# Revit family: Drain_Trench_12_Inch_Wide_Reveal-Zurn-ZF812
name_source: partatom
category: Plumbing Fixtures
units: mm (PartAtom-declared; Revit-internal decimal feet)

## family parameters
Always vertical = Yes
Cut with Voids When Loaded = No
Maintain Annotation Orientation = No
OmniClass Number = 23.70.50.21
OmniClass Title = Liquid Waste Collection and Removal
Part Type = Normal
Room Calculation Point = No
Round Connector Dimension = Use Diameter
Shared = No
Work Plane-Based = No

## types (65) — shared parameters
Approx. Weight (lbs) = 50
Assembly Code = D2040300
Bottom Outlet Connection Extension = 1.063 "
CW Connection = No
Channel Radius Shallow = 3 "
Channel Shallow Radius Exterior = 3.188 "
Connector Thickness 1 = 0.188 "
Description = 12 [305] WIDE REVEAL FIBER REINFORCED POLYMER TRENCH DRAIN SYSTEM WITH STEEL FRAME
Frame Material = Steel - Carbon - Zurn - Painted Black
Grate Material = Iron - Zurn - Cast - Ductile - Painted Black
Grate Thickness = 1.5 "
HW Connection = No
Length = 10 "
Main Material = Polymer - Zurn - Fiber Reinforced - Blue
Manufacturer = Zurn Water, LLC
Manufacurer Brand = Zurn
Model = ZF812
Modified Date = 08/14/2025
Product Documentation Link = https://files.zurn.com
Product Installation Sheet URL = https://files.zurn.com
Product Page URL = https://www.zurn.com
Product data url = https://www.bimobject.com
Trap Primer = No
Type Image = <None>
URL = www.zurn.com
Vent Connection = No
Waste Connection = Yes
angle = 149.00°
zero-valued in all types: CWFU, Default Elevation, HWFU, WFU

## per-type parameters (varying)
| type | Anno-Extension for Endoutlet | Anno-Extension-Deep | Anno-ID | Bottom Connector Length | Bottom Outlet Connection | Deep Invert | End Connector Bottom Length | End Outlet Connection | Flow Rate (GPM) | Outlet Radius | Outlet Radius Exterior | Shallow Invert | Slope Constraints | Trench_Drain-Zurn-ZF812-Bottom_Outlet | Trench_Drain-Zurn-ZF812-End_Outlet | Type Comments |
| ZF812-2002 | 7.992 " | 7.932 " | 2 " | 8.741 " | 2 " | 9.18 " | 9.18 " | 2 " | 937 GPM | 1 " | 1.188 " | 7.93 " | 0.60° | No | No | ZF812-2002 |
| ZF812-2002 W/-E4 | 6.992 " | 7.932 " | 4 " | 8.741 " | 4 " | 9.18 " | 9.18 " | 4 " | 0 GPM | 2 " | 2.188 " | 7.93 " | 0.60° | No | Yes | ZF812-2002 with 4 Inch No-Hub End Outlet |
| ZF812-2002 W/-E6 | 5.992 " | 7.932 " | 6 " | 8.741 " | 6 " | 9.18 " | 9.18 " | 6 " | 0 GPM | 3 " | 3.188 " | 7.93 " | 0.60° | No | Yes | ZF812-2002 with 6 Inch No-Hub End Outlet |
| ZF812-2002 W/-U4 | 6.992 " | 7.932 " | 4 " | 8.741 " | 4 " | 9.18 " | 9.18 " | 4 " | 0 GPM | 2 " | 2.188 " | 7.93 " | 0.60° | Yes | No | ZF812-2002 with 4 Inch No-Hub Bottom Outlet |
| ZF812-2002 W/-U6 | 5.992 " | 7.932 " | 6 " | 8.741 " | 6 " | 9.18 " | 9.18 " | 6 " | 0 GPM | 3 " | 3.188 " | 7.93 " | 0.60° | Yes | No | ZF812-2002 with 6 Inch No-Hub Bottom Outlet |
| ZF812-2002 W/-U8 | 4.992 " | 7.932 " | 8 " | 8.741 " | 8 " | 9.18 " | 9.18 " | 8 " | 0 GPM | 4 " | 4.188 " | 7.93 " | 0.60° | Yes | No | ZF812-2002 with 8 Inch No-Hub Bottom Outlet |
| ZF812-2002N | 7.992 " | 7.932 " | 2 " | 8.741 " | 2 " | 9.18 " | 9.18 " | 2 " | 0 GPM | 1 " | 1.188 " | 9.18 " | 0.00° | No | No | ZF812-2002N |
| ZF812-2003 | 9.242 " | 9.182 " | 2 " | 9.991 " | 2 " | 10.43 " | 10.43 " | 2 " | 1225 GPM | 1 " | 1.188 " | 9.18 " | 0.60° | No | No | ZF812-2003 |
| ZF812-2003 W/-E4 | 8.242 " | 9.182 " | 4 " | 9.991 " | 4 " | 10.43 " | 10.43 " | 4 " | 0 GPM | 2 " | 2.188 " | 9.18 " | 0.60° | No | Yes | ZF812-2003 with 4 Inch No-Hub End Outlet |
| ZF812-2003 W/-E6 | 7.242 " | 9.182 " | 6 " | 9.991 " | 6 " | 10.43 " | 10.43 " | 6 " | 0 GPM | 3 " | 3.188 " | 9.18 " | 0.60° | No | Yes | ZF812-2003 with 6 Inch No-Hub End Outlet |
| ZF812-2003 W/-E8 | 6.242 " | 9.182 " | 8 " | 9.991 " | 8 " | 10.43 " | 10.43 " | 8 " | 0 GPM | 4 " | 4.188 " | 9.18 " | 0.60° | No | Yes | ZF812-2003 with 8 Inch No-Hub End Outlet |
| ZF812-2003 W/-U4 | 8.242 " | 9.182 " | 4 " | 9.991 " | 4 " | 10.43 " | 10.43 " | 4 " | 0 GPM | 2 " | 2.188 " | 9.18 " | 0.60° | Yes | No | ZF812-2003 with 4 Inch No-Hub Bottom Outlet |
| ZF812-2003 W/-U6 | 7.242 " | 9.182 " | 6 " | 9.991 " | 6 " | 10.43 " | 10.43 " | 6 " | 0 GPM | 3 " | 3.188 " | 9.18 " | 0.60° | Yes | No | ZF812-2003 with 6 Inch No-Hub Bottom Outlet |
| ZF812-2003 W/-U8 | 6.242 " | 9.182 " | 8 " | 9.991 " | 8 " | 10.43 " | 10.43 " | 8 " | 0 GPM | 4 " | 4.188 " | 9.18 " | 0.60° | Yes | No | ZF812-2003 with 8 Inch No-Hub Bottom Outlet |
| ZF812-2004 | 10.492 " | 10.432 " | 2 " | 11.241 " | 2 " | 11.68 " | 11.68 " | 2 " | 1521 GPM | 1 " | 1.188 " | 10.43 " | 0.60° | No | No | ZF812-2004 |
| ZF812-2004 W/-E4 | 9.492 " | 10.432 " | 4 " | 11.241 " | 4 " | 11.68 " | 11.68 " | 4 " | 0 GPM | 2 " | 2.188 " | 10.43 " | 0.60° | No | Yes | ZF812-2004 with 4 Inch No-Hub End Outlet |
| ZF812-2004 W/-E6 | 8.492 " | 10.432 " | 6 " | 11.241 " | 6 " | 11.68 " | 11.68 " | 6 " | 0 GPM | 3 " | 3.188 " | 10.43 " | 0.60° | No | Yes | ZF812-2004 with 6 Inch No-Hub End Outlet |
| ZF812-2004 W/-E8 | 7.492 " | 10.432 " | 8 " | 11.241 " | 8 " | 11.68 " | 11.68 " | 8 " | 0 GPM | 4 " | 4.188 " | 10.43 " | 0.60° | No | Yes | ZF812-2004 with 8 Inch No-Hub End Outlet |
| ZF812-2004 W/-U4 | 9.492 " | 10.432 " | 4 " | 11.241 " | 4 " | 11.68 " | 11.68 " | 4 " | 0 GPM | 2 " | 2.188 " | 10.43 " | 0.60° | Yes | No | ZF812-2004 with 4 Inch No-Hub Bottom Outlet |
| ZF812-2004 W/-U6 | 8.492 " | 10.432 " | 6 " | 11.241 " | 6 " | 11.68 " | 11.68 " | 6 " | 0 GPM | 3 " | 3.188 " | 10.43 " | 0.60° | Yes | No | ZF812-2004 with 6 Inch No-Hub Bottom Outlet |
| ZF812-2004 W/-U8 | 7.492 " | 10.432 " | 8 " | 11.241 " | 8 " | 11.68 " | 11.68 " | 8 " | 0 GPM | 4 " | 4.188 " | 10.43 " | 0.60° | Yes | No | ZF812-2004 with 8 Inch No-Hub Bottom Outlet |
| ZF812-2004N | 10.492 " | 10.432 " | 2 " | 11.241 " | 2 " | 11.68 " | 11.68 " | 2 " | 0 GPM | 1 " | 1.188 " | 11.68 " | 0.00° | No | No | ZF812-2004N |
| ZF812-2005 | 11.742 " | 11.682 " | 2 " | 12.491 " | 2 " | 12.93 " | 12.93 " | 2 " | 1821 GPM | 1 " | 1.188 " | 11.68 " | 0.60° | No | No | ZF812-2005 |
| ZF812-2005 W/-E4 | 10.742 " | 11.682 " | 4 " | 12.491 " | 4 " | 12.93 " | 12.93 " | 4 " | 0 GPM | 2 " | 2.188 " | 11.68 " | 0.60° | No | Yes | ZF812-2005 with 4 Inch No-Hub End Outlet |
| ZF812-2005 W/-E6 | 9.742 " | 11.682 " | 6 " | 12.491 " | 6 " | 12.93 " | 12.93 " | 6 " | 0 GPM | 3 " | 3.188 " | 11.68 " | 0.60° | No | Yes | ZF812-2005 with 6 Inch No-Hub End Outlet |
| ZF812-2005 W/-E8 | 8.742 " | 11.682 " | 8 " | 12.491 " | 8 " | 12.93 " | 12.93 " | 8 " | 0 GPM | 4 " | 4.188 " | 11.68 " | 0.60° | No | Yes | ZF812-2005 with 8 Inch No-Hub End Outlet |
| ZF812-2005 W/-U4 | 10.742 " | 11.682 " | 4 " | 12.491 " | 4 " | 12.93 " | 12.93 " | 4 " | 0 GPM | 2 " | 2.188 " | 11.68 " | 0.60° | Yes | No | ZF812-2005 with 4 Inch No-Hub Bottom Outlet |
| ZF812-2005 W/-U6 | 9.742 " | 11.682 " | 6 " | 12.491 " | 6 " | 12.93 " | 12.93 " | 6 " | 0 GPM | 3 " | 3.188 " | 11.68 " | 0.60° | Yes | No | ZF812-2005 with 6 Inch No-Hub Bottom Outlet |
| ZF812-2005 W/-U8 | 8.742 " | 11.682 " | 8 " | 12.491 " | 8 " | 12.93 " | 12.93 " | 8 " | 0 GPM | 4 " | 4.188 " | 11.68 " | 0.60° | Yes | No | ZF812-2005 with 8 Inch No-Hub Bottom Outlet |
| ZF812-2006 | 12.992 " | 12.932 " | 2 " | 13.741 " | 2 " | 14.18 " | 14.18 " | 2 " | 2125 GPM | 1 " | 1.188 " | 12.93 " | 0.60° | No | No | ZF812-2006 |
| ZF812-2006 W/-E4 | 11.992 " | 12.932 " | 4 " | 13.741 " | 4 " | 14.18 " | 14.18 " | 4 " | 0 GPM | 2 " | 2.188 " | 12.93 " | 0.60° | No | Yes | ZF812-2006 with 4 Inch No-Hub End Outlet |
| ZF812-2006 W/-E6 | 10.992 " | 12.932 " | 6 " | 13.741 " | 6 " | 14.18 " | 14.18 " | 6 " | 0 GPM | 3 " | 3.188 " | 12.93 " | 0.60° | No | Yes | ZF812-2006 with 6 Inch No-Hub End Outlet |
| ZF812-2006 W/-E8 | 9.992 " | 12.932 " | 8 " | 13.741 " | 8 " | 14.18 " | 14.18 " | 8 " | 0 GPM | 4 " | 4.188 " | 12.93 " | 0.60° | No | Yes | ZF812-2006 with 8 Inch No-Hub End Outlet |
| ZF812-2006 W/-U4 | 11.992 " | 12.932 " | 4 " | 13.741 " | 4 " | 14.18 " | 14.18 " | 4 " | 0 GPM | 2 " | 2.188 " | 12.93 " | 0.60° | Yes | No | ZF812-2006 with 4 Inch No-Hub Bottom Outlet |
| ZF812-2006 W/-U6 | 10.992 " | 12.932 " | 6 " | 13.741 " | 6 " | 14.18 " | 14.18 " | 6 " | 0 GPM | 3 " | 3.188 " | 12.93 " | 0.60° | Yes | No | ZF812-2006 with 6 Inch No-Hub Bottom Outlet |
| ZF812-2006 W/-U8 | 9.992 " | 12.932 " | 8 " | 13.741 " | 8 " | 14.18 " | 14.18 " | 8 " | 0 GPM | 4 " | 4.188 " | 12.93 " | 0.60° | Yes | No | ZF812-2006 with 8 Inch No-Hub Bottom Outlet |
| ZF812-2007 | 14.242 " | 14.182 " | 2 " | 14.991 " | 2 " | 15.43 " | 15.43 " | 2 " | 2432 GPM | 1 " | 1.188 " | 14.18 " | 0.60° | No | No | ZF812-2007 |
| ZF812-2007 W/-E4 | 13.242 " | 14.182 " | 4 " | 14.991 " | 4 " | 15.43 " | 15.43 " | 4 " | 0 GPM | 2 " | 2.188 " | 14.18 " | 0.60° | No | Yes | ZF812-2007 with 4 Inch No-Hub End Outlet |
| ZF812-2007 W/-E6 | 12.242 " | 14.182 " | 6 " | 14.991 " | 6 " | 15.43 " | 15.43 " | 6 " | 0 GPM | 3 " | 3.188 " | 14.18 " | 0.60° | No | Yes | ZF812-2007 with 6 Inch No-Hub End Outlet |
| ZF812-2007 W/-E8 | 11.242 " | 14.182 " | 8 " | 14.991 " | 8 " | 15.43 " | 15.43 " | 8 " | 0 GPM | 4 " | 4.188 " | 14.18 " | 0.60° | No | Yes | ZF812-2007 with 8 Inch No-Hub End Outlet |
| ZF812-2007 W/-U4 | 13.242 " | 14.182 " | 4 " | 14.991 " | 4 " | 15.43 " | 15.43 " | 4 " | 0 GPM | 2 " | 2.188 " | 14.18 " | 0.60° | Yes | No | ZF812-2007 with 4 Inch No-Hub Bottom Outlet |
| ZF812-2007 W/-U6 | 12.242 " | 14.182 " | 6 " | 14.991 " | 6 " | 15.43 " | 15.43 " | 6 " | 0 GPM | 3 " | 3.188 " | 14.18 " | 0.60° | Yes | No | ZF812-2007 with 6 Inch No-Hub Bottom Outlet |
| ZF812-2007 W/-U8 | 11.242 " | 14.182 " | 8 " | 14.991 " | 8 " | 15.43 " | 15.43 " | 8 " | 0 GPM | 4 " | 4.188 " | 14.18 " | 0.60° | Yes | No | ZF812-2007 with 8 Inch No-Hub Bottom Outlet |
| ZF812-2008 | 15.492 " | 15.432 " | 2 " | 16.241 " | 2 " | 16.68 " | 16.68 " | 2 " | 2742 GPM | 1 " | 1.188 " | 15.43 " | 0.60° | No | No | ZF812-2008 |
| ZF812-2008 W/-E4 | 14.492 " | 15.432 " | 4 " | 16.241 " | 4 " | 16.68 " | 16.68 " | 4 " | 0 GPM | 2 " | 2.188 " | 15.43 " | 0.60° | No | Yes | ZF812-2008 with 4 Inch No-Hub End Outlet |
| ZF812-2008 W/-E6 | 13.492 " | 15.432 " | 6 " | 16.241 " | 6 " | 16.68 " | 16.68 " | 6 " | 0 GPM | 3 " | 3.188 " | 15.43 " | 0.60° | No | Yes | ZF812-2008 with 6 Inch No-Hub End Outlet |
| ZF812-2008 W/-E8 | 12.492 " | 15.432 " | 8 " | 16.241 " | 8 " | 16.68 " | 16.68 " | 8 " | 0 GPM | 4 " | 4.188 " | 15.43 " | 0.60° | No | Yes | ZF812-2008 with 8 Inch No-Hub End Outlet |
| ZF812-2008 W/-U4 | 14.492 " | 15.432 " | 4 " | 16.241 " | 4 " | 16.68 " | 16.68 " | 4 " | 0 GPM | 2 " | 2.188 " | 15.43 " | 0.60° | Yes | No | ZF812-2008 with 4 Inch No-Hub Bottom Outlet |
| ZF812-2008 W/-U6 | 13.492 " | 15.432 " | 6 " | 16.241 " | 6 " | 16.68 " | 16.68 " | 6 " | 0 GPM | 3 " | 3.188 " | 15.43 " | 0.60° | Yes | No | ZF812-2008 with 6 Inch No-Hub Bottom Outlet |
| ZF812-2008 W/-U8 | 12.492 " | 15.432 " | 8 " | 16.241 " | 8 " | 16.68 " | 16.68 " | 8 " | 0 GPM | 4 " | 4.188 " | 15.43 " | 0.60° | Yes | No | ZF812-2008 with 8 Inch No-Hub Bottom Outlet |
| ZF812-2008N | 15.492 " | 15.432 " | 2 " | 16.241 " | 2 " | 16.68 " | 16.68 " | 2 " | 0 GPM | 1 " | 1.188 " | 16.68 " | 0.00° | No | No | ZF812-2008N |
| ZF812-2009 | 16.742 " | 16.682 " | 2 " | 17.491 " | 2 " | 17.93 " | 17.93 " | 2 " | 3053 GPM | 1 " | 1.188 " | 16.68 " | 0.60° | No | No | ZF812-2009 |
| ZF812-2009 W/-E4 | 15.742 " | 16.682 " | 4 " | 17.491 " | 4 " | 17.93 " | 17.93 " | 4 " | 0 GPM | 2 " | 2.188 " | 16.68 " | 0.60° | No | Yes | ZF812-2009 with 4 Inch No-Hub End Outlet |
| ZF812-2009 W/-E6 | 14.742 " | 16.682 " | 6 " | 17.491 " | 6 " | 17.93 " | 17.93 " | 6 " | 0 GPM | 3 " | 3.188 " | 16.68 " | 0.60° | No | Yes | ZF812-2009 with 6 Inch No-Hub End Outlet |
| ZF812-2009 W/-E8 | 13.742 " | 16.682 " | 8 " | 17.491 " | 8 " | 17.93 " | 17.93 " | 8 " | 0 GPM | 4 " | 4.188 " | 16.68 " | 0.60° | No | Yes | ZF812-2009 with 8 Inch No-Hub End Outlet |
| ZF812-2009 W/-U4 | 15.742 " | 16.682 " | 4 " | 17.491 " | 4 " | 17.93 " | 17.93 " | 4 " | 0 GPM | 2 " | 2.188 " | 16.68 " | 0.60° | Yes | No | ZF812-2009 with 4 Inch No-Hub Bottom Outlet |
| ZF812-2009 W/-U6 | 14.742 " | 16.682 " | 6 " | 17.491 " | 6 " | 17.93 " | 17.93 " | 6 " | 0 GPM | 3 " | 3.188 " | 16.68 " | 0.60° | Yes | No | ZF812-2009 with 6 Inch No-Hub Bottom Outlet |
| ZF812-2009 W/-U8 | 13.742 " | 16.682 " | 8 " | 17.491 " | 8 " | 17.93 " | 17.93 " | 8 " | 0 GPM | 4 " | 4.188 " | 16.68 " | 0.60° | Yes | No | ZF812-2009 with 8 Inch No-Hub Bottom Outlet |
| ZF812-2010 | 17.992 " | 17.932 " | 2 " | 18.741 " | 2 " | 19.18 " | 19.18 " | 2 " | 3365 GPM | 1 " | 1.188 " | 17.93 " | 0.60° | No | No | ZF812-2010 |
| ZF812-2010 W/-E4 | 16.992 " | 17.932 " | 4 " | 18.741 " | 4 " | 19.18 " | 19.18 " | 4 " | 0 GPM | 2 " | 2.188 " | 17.93 " | 0.60° | No | Yes | ZF812-2010 with 4 Inch No-Hub End Outlet |
| ZF812-2010 W/-E6 | 15.992 " | 17.932 " | 6 " | 18.741 " | 6 " | 19.18 " | 19.18 " | 6 " | 0 GPM | 3 " | 3.188 " | 17.93 " | 0.60° | No | Yes | ZF812-2010 with 6 Inch No-Hub End Outlet |
| ZF812-2010 W/-E8 | 14.992 " | 17.932 " | 8 " | 18.741 " | 8 " | 19.18 " | 19.18 " | 8 " | 0 GPM | 4 " | 4.188 " | 17.93 " | 0.60° | No | Yes | ZF812-2010 with 8 Inch No-Hub End Outlet |
| ZF812-2010 W/-U4 | 16.992 " | 17.932 " | 4 " | 18.741 " | 4 " | 19.18 " | 19.18 " | 4 " | 0 GPM | 2 " | 2.188 " | 17.93 " | 0.60° | Yes | No | ZF812-2010 with 4 Inch No-Hub Bottom Outlet |
| ZF812-2010 W/-U6 | 15.992 " | 17.932 " | 6 " | 18.741 " | 6 " | 19.18 " | 19.18 " | 6 " | 0 GPM | 3 " | 3.188 " | 17.93 " | 0.60° | Yes | No | ZF812-2010 with 6 Inch No-Hub Bottom Outlet |
| ZF812-2010 W/-U8 | 14.992 " | 17.932 " | 8 " | 18.741 " | 8 " | 19.18 " | 19.18 " | 8 " | 0 GPM | 4 " | 4.188 " | 17.93 " | 0.60° | Yes | No | ZF812-2010 with 8 Inch No-Hub Bottom Outlet |

## geometry (parser evidence)
native form markers: Blend x18, Sweep x13
no freeform markers — native parametric forms only
